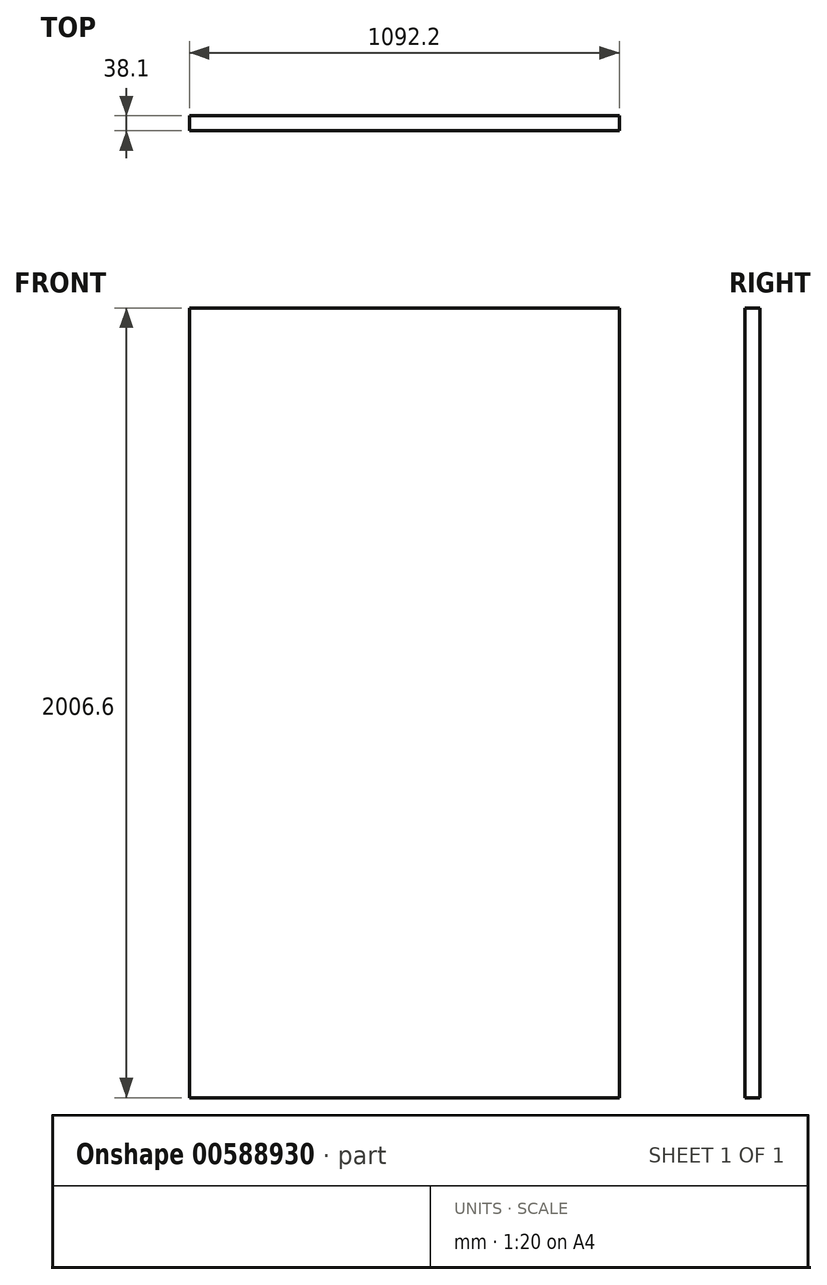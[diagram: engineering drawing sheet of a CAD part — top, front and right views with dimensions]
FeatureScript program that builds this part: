
annotation { "Feature Type Name" : "Feature", "Feature Type Description" : "" }
export const myFeature = defineFeature(function(context is Context, id is Id, definition is map)
    precondition{}
    {
        {
            var Q0;
            Q0=qCreatedBy(makeId("Front.planeOp"),FACE);
            var sketch = newSketch(context, id + "F0", { "sketchPlane" : qUnion([Q0])});
            skLineSegment(sketch, "E0.bottom", {"start": v(0, 0) * mm, "end": v(-1092.2, 0) * mm});
            skLineSegment(sketch, "E0.top", {"start": v(0, 2006.6) * mm, "end": v(-1092.2, 2006.6) * mm});
            skLineSegment(sketch, "E0.left", {"start": v(0, 0) * mm, "end": v(0, 2006.6) * mm});
            skLineSegment(sketch, "E0.right", {"start": v(-1092.2, 0) * mm, "end": v(-1092.2, 2006.6) * mm});
            skSolve(sketch);
        }
        {
            var Q0;
            Q0 = qSketchRegion(id + "F0", true);
            extrude(context, id + "F1", {"entities" : qUnion([Q0]), "depth" : 38.1 * mm, "offsetDistance" : 25.4 * mm});
        }
    });
